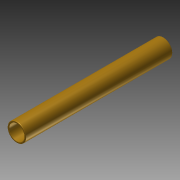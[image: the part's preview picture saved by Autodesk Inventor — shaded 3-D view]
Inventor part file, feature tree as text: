
AUTODESK INVENTOR PART (.ipt)
format: ipt  version: 2011 SP1 (Build 150282100, 282)  size: 93,184 bytes
history: native  units: in
note: dims shown in document units (in); Inventor stores cm internally (conversion verified against a paired STEP export)
features: extrude x1, fillet x1, sketch x1
ambient origin geometry x8: Origin, YZ Plane, XZ Plane, XY Plane, X Axis, Y Axis, Z Axis, Center Point
bodies: Solid1 (feature_tree)
feature tree (3):
  extrude  "Extrusion1"  Depth=0.016in
  fillet  "Fillet1"  Radius=1.5in
  sketch  "Sketch1"  dims[d0=0.187in d1=0.016in d2=1.5in d3=0.0in d4=0.005in]
